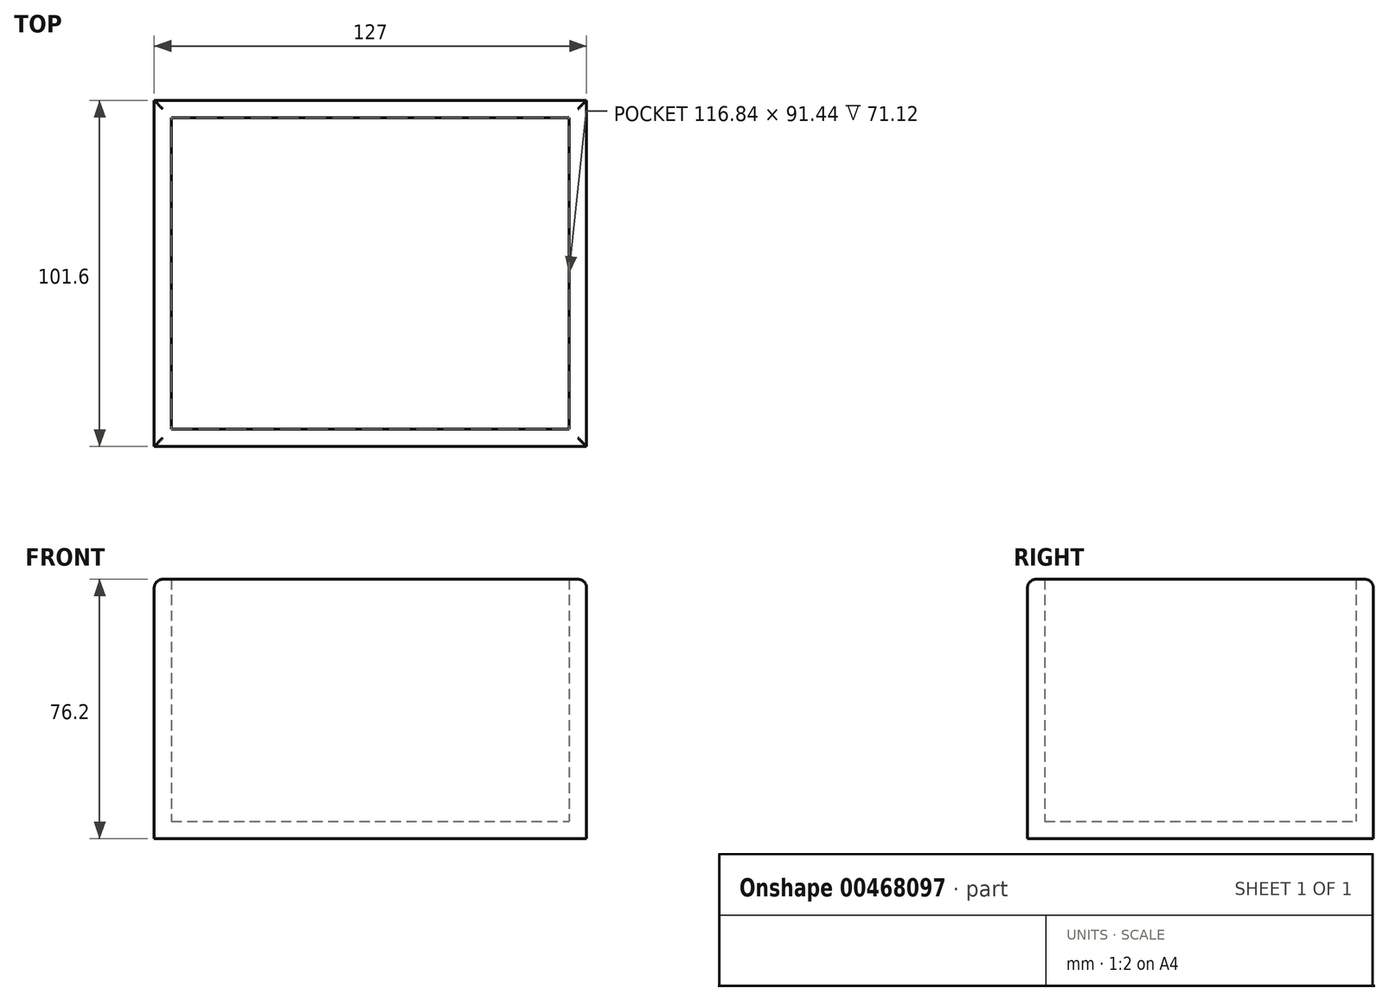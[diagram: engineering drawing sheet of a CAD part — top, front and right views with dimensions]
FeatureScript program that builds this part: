
annotation { "Feature Type Name" : "Feature", "Feature Type Description" : "" }
export const myFeature = defineFeature(function(context is Context, id is Id, definition is map)
    precondition{}
    {
        {
            var Q0;
            Q0=qCreatedBy(makeId("Front.planeOp"),FACE);
            var sketch = newSketch(context, id + "F0", { "sketchPlane" : qUnion([Q0])});
            skLineSegment(sketch, "E0.bottom", {"start": v(-69.65, 26.78) * mm, "end": v(57.35, 26.78) * mm});
            skLineSegment(sketch, "E0.top", {"start": v(-69.65, -49.42) * mm, "end": v(57.35, -49.42) * mm});
            skLineSegment(sketch, "E0.left", {"start": v(-69.65, 26.78) * mm, "end": v(-69.65, -49.42) * mm});
            skLineSegment(sketch, "E0.right", {"start": v(57.35, 26.78) * mm, "end": v(57.35, -49.42) * mm});
            skSolve(sketch);
        }
        {
            var Q0;
            Q0 = qSketchRegion(id + "F0", true);
            extrude(context, id + "F1", {"entities" : qUnion([Q0]), "depth" : 101.6 * mm});
        }
        {
            var Q0;
            Q0=makeQuery(id+"F1.opExtrude","SWEPT_FACE",FACE,{"disambiguationData":[OSD([sQuery(id+"F0.wireOp",EDGE,"E0.bottom")])]});
            shell(context, id + "F2", {"entities" : qUnion([Q0]), "thickness" : 5.08 * mm});
        }
        {
            var Q0;
            Q0=makeQuery(id+"F1.opExtrude","CAP_EDGE",EDGE,{"disambiguationData":[OSD([sQuery(id+"F0.wireOp",EDGE,"E0.bottom")])],"isStart":false});
            var Q1;
            Q1=makeQuery(id+"F1.opExtrude","SWEPT_EDGE",EDGE,{"disambiguationData":[OSD([sQuery(id+"F0.wireOp",EDGE,"E0.bottom"),sQuery(id+"F0.wireOp",EDGE,"E0.left")])]});
            var Q2;
            Q2=makeQuery(id+"F1.opExtrude","CAP_EDGE",EDGE,{"disambiguationData":[OSD([sQuery(id+"F0.wireOp",EDGE,"E0.bottom")])],"isStart":true});
            var Q3;
            Q3=makeQuery(id+"F1.opExtrude","SWEPT_EDGE",EDGE,{"disambiguationData":[OSD([sQuery(id+"F0.wireOp",EDGE,"E0.bottom"),sQuery(id+"F0.wireOp",EDGE,"E0.right")])]});
            fillet(context, id + "F3", {"entities" : qUnion([Q0, Q1, Q2, Q3]), "radius" : 2.54 * mm, "tangentPropagation" : true, "allowEdgeOverflow" : false});
        }
    });
